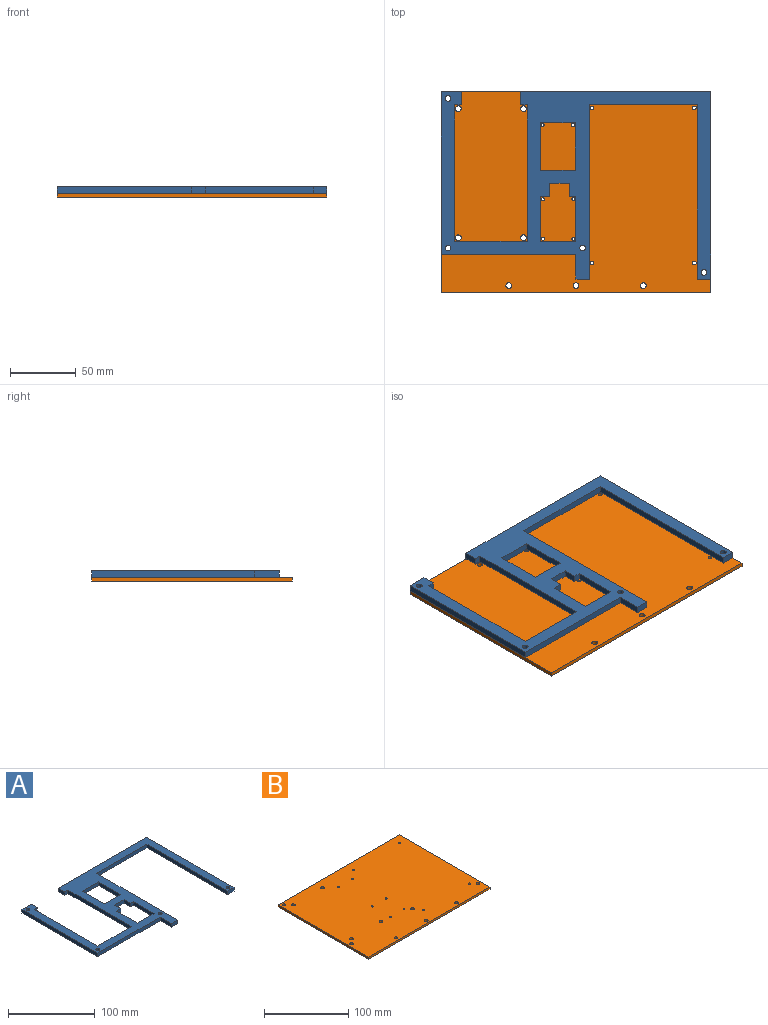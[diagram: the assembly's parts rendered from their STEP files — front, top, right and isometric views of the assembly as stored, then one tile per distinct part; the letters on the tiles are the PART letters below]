
ASSEMBLY  parts=2 mates=1
PART A: 36 faces, bbox 204x142x5 mm
  f0: plane 103.5x5mm, normal (-1,0,0), area 517.5mm2, adj f1,f30,f34,f35
  f1: plane 55x5mm, normal (0,1,0), area 275mm2, adj f0,f2,f34,f35
  f2: plane 103.5x5mm, normal (1,0,0), area 517.5mm2, adj f1,f3,f34,f35
  f3: plane 5x5mm, normal (0,-1,0), area 25mm2, adj f2,f4,f34,f35
  f4: plane 10x5mm, normal (1,0,0), area 50mm2, adj f3,f5,f34,f35
  f5: plane 15x5mm, normal (0,1,0), area 75mm2, adj f4,f6,f34,f35
  f6: plane 123.5x5mm, normal (-1,0,0), area 617.5mm2, adj f5,f7,f34,f35
  f7: plane 102x5mm, normal (0,-1,0), area 510mm2, adj f6,f8,f34,f35
  f8: plane 18.5x5mm, normal (-1,0,0), area 92.5mm2, adj f7,f9,f34,f35
  f9: plane 10x5mm, normal (0,-1,0), area 50mm2, adj f8,f10,f34,f35
  f10: plane 132x5mm, normal (1,0,0), area 660mm2, adj f9,f11,f34,f35
  f11: plane 82x5mm, normal (0,-1,0), area 410mm2, adj f10,f12,f34,f35
  f12: plane 132x5mm, normal (-1,0,0), area 660mm2, adj f11,f13,f34,f35
  f13: plane 10x5mm, normal (0,-1,0), area 50mm2, adj f12,f14,f34,f35
  f14: plane 142x5mm, normal (1,0,0), area 710mm2, adj f13,f15,f34,f35
  f15: plane 144x5mm, normal (0,1,0), area 720mm2, adj f14,f16,f34,f35
  f16: plane 10x5mm, normal (-1,0,0), area 50mm2, adj f15,f30,f34,f35
  f17: plane 26.5x5mm, normal (0,1,0), area 132.5mm2, adj f18,f31,f34,f35
  f18: plane 36x5mm, normal (1,0,0), area 180mm2, adj f17,f19,f34,f35
  f19: plane 26.5x5mm, normal (0,-1,0), area 132.5mm2, adj f18,f31,f34,f35
  f20: plane 27x5mm, normal (0,1,0), area 135mm2, adj f21,f32,f34,f35
  f21: plane 34x5mm, normal (1,0,0), area 170mm2, adj f20,f22,f34,f35
  f22: plane 7x5mm, normal (0,-1,0), area 35mm2, adj f21,f23,f34,f35
  f23: plane 10x5mm, normal (1,0,0), area 50mm2, adj f22,f24,f34,f35
  f24: plane 15x5mm, normal (0,-1,0), area 75mm2, adj f23,f25,f34,f35
  f25: plane 10x5mm, normal (-1,0,0), area 50mm2, adj f24,f26,f34,f35
  f26: plane 5x5mm, normal (0,-1,0), area 25mm2, adj f25,f32,f34,f35
  f27: cylinder r=2.15mm len=5mm, axis (0,0,-1), area 67.5mm2, adj f34,f35
  f28: cylinder r=2.15mm len=5mm, axis (0,0,-1), area 67.5mm2, adj f34,f35
  f29: cylinder r=2.15mm len=5mm, axis (0,0,-1), area 67.5mm2, adj f34,f35
  f30: plane 5x5mm, normal (0,-1,0), area 25mm2, adj f0,f16,f34,f35
  f31: plane 36x5mm, normal (-1,0,0), area 180mm2, adj f17,f19,f34,f35
  f32: plane 34x5mm, normal (-1,0,0), area 170mm2, adj f20,f26,f34,f35
  f33: cylinder r=2.15mm len=5mm, axis (0,0,-1), area 67.5mm2, adj f34,f35
  f34: plane 204x142mm, normal (0,0,1), area 8034.4mm2, adj f0,f1,f2,f3,f4,f5,f6,f7
  f35: plane 204x142mm, normal (0,0,-1), area 8034.4mm2, adj f0,f1,f2,f3,f4,f5,f6,f7
PART B: 27 faces, bbox 204x152x3 mm
  f0: plane 152x3mm, normal (-1,0,0), area 456mm2, adj f1,f21,f25,f26
  f1: plane 204x3mm, normal (0,-1,0), area 612mm2, adj f0,f2,f25,f26
  f2: plane 152x3mm, normal (1,0,0), area 456mm2, adj f1,f21,f25,f26
  f3: cylinder r=1.2mm len=3mm, axis (0,0,-1), area 22.6mm2, adj f25,f26
  f4: cylinder r=1.15mm len=3mm, axis (0,0,-1), area 21.7mm2, adj f25,f26
  f5: cylinder r=1.15mm len=3mm, axis (0,0,-1), area 21.7mm2, adj f25,f26
  f6: cylinder r=1.15mm len=3mm, axis (0,0,-1), area 21.7mm2, adj f25,f26
  f7: cylinder r=1.15mm len=3mm, axis (0,0,-1), area 21.7mm2, adj f25,f26
  f8: cylinder r=2.15mm len=4.3mm, axis (0,0,-1), area 40.5mm2, adj f25,f26
  f9: cylinder r=2.15mm len=4.3mm, axis (0,0,-1), area 40.5mm2, adj f25,f26
  f10: cylinder r=2.15mm len=4.3mm, axis (0,0,-1), area 40.5mm2, adj f25,f26
  f11: cylinder r=2.15mm len=4.3mm, axis (0,0,-1), area 40.5mm2, adj f25,f26
  f12: cylinder r=2.15mm len=4.3mm, axis (0,0,-1), area 40.5mm2, adj f25,f26
  f13: cylinder r=2.15mm len=4.3mm, axis (0,0,-1), area 40.5mm2, adj f25,f26
  f14: cylinder r=2.15mm len=4.3mm, axis (0,0,-1), area 40.5mm2, adj f25,f26
  f15: cylinder r=1.4mm len=3mm, axis (0,0,-1), area 26.4mm2, adj f25,f26
  f16: cylinder r=1.4mm len=3mm, axis (0,0,-1), area 26.4mm2, adj f25,f26
  f17: cylinder r=1.4mm len=3mm, axis (0,0,-1), area 26.4mm2, adj f25,f26
  f18: cylinder r=1.4mm len=3mm, axis (0,0,-1), area 26.4mm2, adj f25,f26
  f19: cylinder r=2.15mm len=4.3mm, axis (0,0,-1), area 40.5mm2, adj f25,f26
  f20: cylinder r=2.15mm len=4.3mm, axis (0,0,-1), area 40.5mm2, adj f25,f26
  f21: plane 204x3mm, normal (0,1,0), area 612mm2, adj f0,f2,f25,f26
  f22: cylinder r=2.15mm len=4.3mm, axis (0,0,-1), area 40.5mm2, adj f25,f26
  f23: cylinder r=2.15mm len=4.3mm, axis (0,0,-1), area 40.5mm2, adj f25,f26
  f24: cylinder r=1.2mm len=3mm, axis (0,0,-1), area 22.6mm2, adj f25,f26
  f25: plane 204x152mm, normal (0,0,1), area 30798mm2, adj f0,f1,f2,f3,f4,f5,f6,f7
  f26: plane 204x152mm, normal (0,0,-1), area 30798mm2, adj f0,f1,f2,f3,f4,f5,f6,f7
PLACE A t=(37.43,77.26,-34.57)mm
PLACE B t=(37.43,78.26,-37.57)mm
MATE fastened A.f35 <-> B.f25  axis (0,0,-1) through (-101.92,76,-34.57)mm
